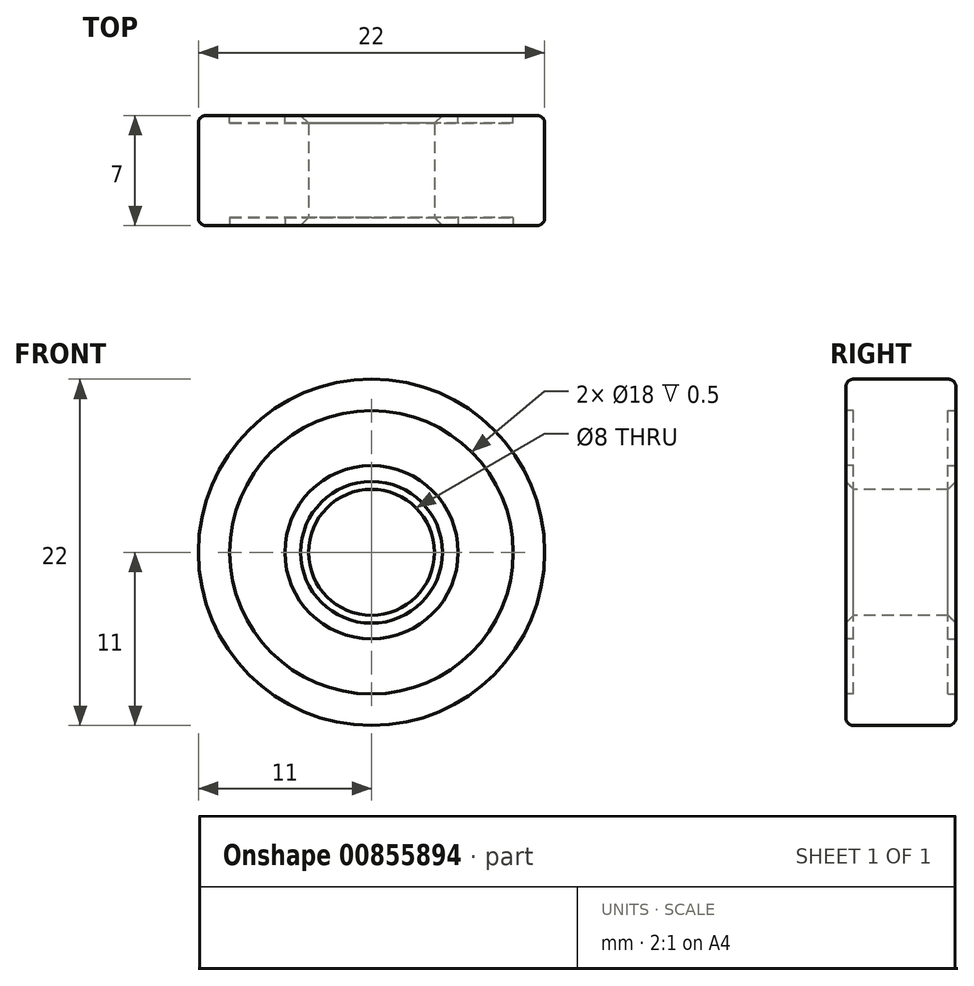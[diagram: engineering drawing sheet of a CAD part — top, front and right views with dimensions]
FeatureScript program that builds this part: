
annotation { "Feature Type Name" : "Feature", "Feature Type Description" : "" }
export const myFeature = defineFeature(function(context is Context, id is Id, definition is map)
    precondition{}
    {
        {
            var Q0;
            Q0=qCreatedBy(makeId("Right.planeOp"),FACE);
            var sketch = newSketch(context, id + "F0", { "sketchPlane" : qUnion([Q0])});
            skLineSegment(sketch, "E0", {"start": v(-3.5, 4) * mm, "end": v(3.5, 4) * mm});
            skLineSegment(sketch, "E1", {"start": v(3.5, 4) * mm, "end": v(3.5, 10.5) * mm});
            skLineSegment(sketch, "E2", {"start": v(3, 11) * mm, "end": v(-3, 11) * mm});
            skLineSegment(sketch, "E3", {"start": v(-3.5, 10.5) * mm, "end": v(-3.5, 4) * mm});
            skPoint(sketch, "E4.visualSharp", {"position": v(-3.5, 11) * mm});
            skArc(sketch, "E4.filletArc", {"start": v(-3, 11) * mm, "mid": v(-3.35, 10.85) * mm, "end": v(-3.5, 10.5) * mm});
            skPoint(sketch, "E5.visualSharp", {"position": v(3.5, 11) * mm});
            skArc(sketch, "E5.filletArc", {"start": v(3.5, 10.5) * mm, "mid": v(3.35, 10.85) * mm, "end": v(3, 11) * mm});
            skLineSegment(sketch, "E6", {"start": v(-7.89, 0) * mm, "end": v(11.78, 0) * mm, "construction": true});
            skSolve(sketch);
        }
        {
            var Q0;
            Q0=qSketchRegion(id+"F0",true);
            var Q1;
            Q1=sQuery(id+"F0.wireOp",EDGE,"E6");
            revolve(context, id + "F1", {"surfaceOperationType" : NewSurfaceOperationType.NEW, "entities" : qUnion([Q0]), "axis" : qUnion([Q1]), "revolveType" : RevolveType.FULL});
        }
        {
            var Q0;
            Q0=makeQuery(id+"F1.opRevolve","SWEPT_EDGE",EDGE,{"disambiguationData":[OSD([sQuery(id+"F0.wireOp",EDGE,"E0"),sQuery(id+"F0.wireOp",EDGE,"E1")])]});
            var Q1;
            Q1=makeQuery(id+"F1.opRevolve","SWEPT_EDGE",EDGE,{"disambiguationData":[OSD([sQuery(id+"F0.wireOp",EDGE,"E0"),sQuery(id+"F0.wireOp",EDGE,"E3")])]});
            chamfer(context, id + "F2", {"entities" : qUnion([Q0, Q1]), "width" : 0.5 * mm, "tangentPropagation" : true});
        }
        {
            var Q0;
            Q0=qCreatedBy(makeId("Front.planeOp"),FACE);
            cPlane(context, id + "F3", {"entities" : qUnion([Q0]), "cplaneType" : CPlaneType.OFFSET, "offset" : 5 * mm, "width" : 150 * mm, "height" : 150 * mm});
        }
        {
            var Q0;
            Q0=qCreatedBy(makeId("Front.planeOp"),FACE);
            cPlane(context, id + "F4", {"entities" : qUnion([Q0]), "cplaneType" : CPlaneType.OFFSET, "offset" : 5 * mm, "oppositeDirection" : true, "width" : 150 * mm, "height" : 150 * mm});
        }
        {
            var Q0;
            Q0=qCreatedBy(id+"F4.planeOp",FACE);
            var sketch = newSketch(context, id + "F5", { "sketchPlane" : qUnion([Q0])});
            skCircle(sketch, "E7", {"center": v(0, 0) * mm, "radius": 9 * mm});
            skCircle(sketch, "E8", {"center": v(0, 0) * mm, "radius": 5.5 * mm});
            skSolve(sketch);
        }
        {
            var Q0;
            Q0=qSketchRegion(id+"F5",true);
            extrude(context, id + "F6", {"entities" : qUnion([Q0]), "operationType" : NewBodyOperationType.REMOVE, "depth" : 2 * mm, "offsetDistance" : 25 * mm});
        }
        {
            var Q0;
            Q0=qCreatedBy(id+"F3.planeOp",FACE);
            var sketch = newSketch(context, id + "F7", { "sketchPlane" : qUnion([Q0])});
            skCircle(sketch, "E9", {"center": v(0, 0) * mm, "radius": 5.5 * mm});
            skCircle(sketch, "E10", {"center": v(0, 0) * mm, "radius": 9 * mm});
            skSolve(sketch);
        }
        {
            var Q0;
            Q0=qSketchRegion(id+"F7",true);
            extrude(context, id + "F8", {"entities" : qUnion([Q0]), "operationType" : NewBodyOperationType.REMOVE, "oppositeDirection" : true, "depth" : 2 * mm, "offsetDistance" : 25 * mm});
        }
    });
